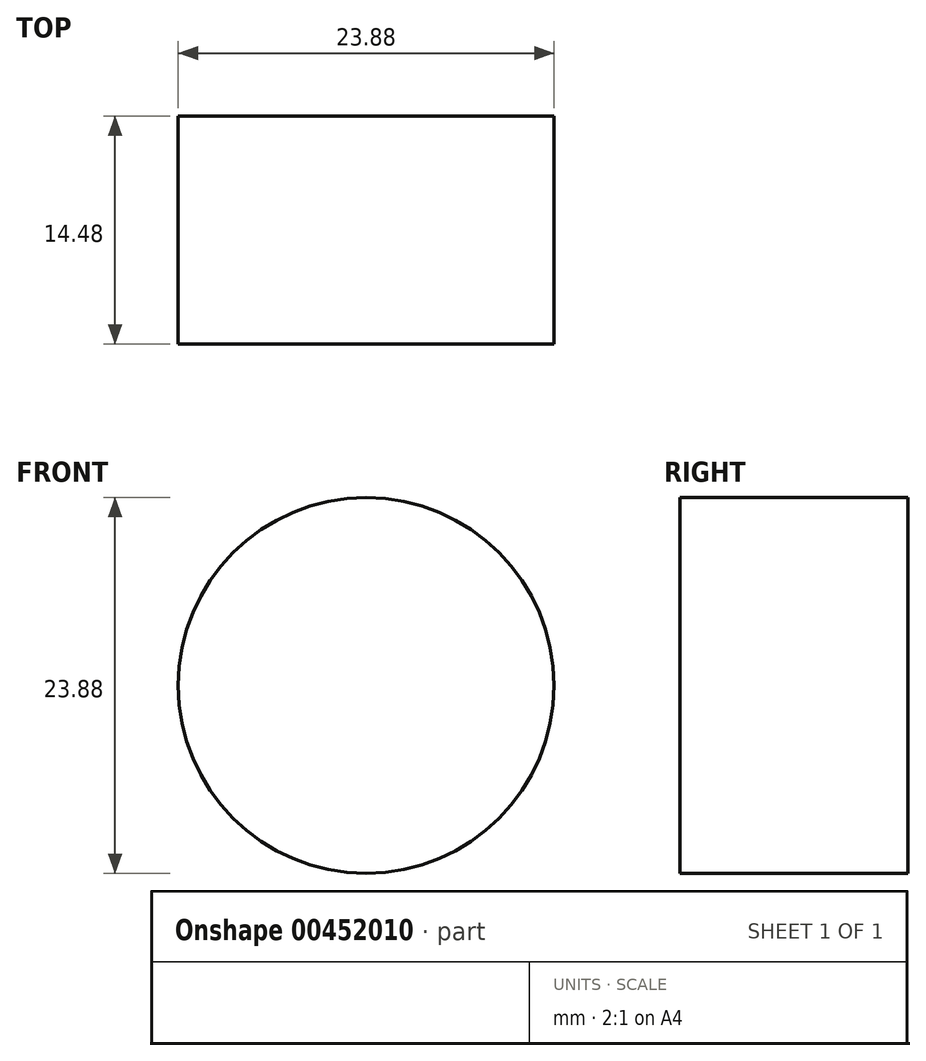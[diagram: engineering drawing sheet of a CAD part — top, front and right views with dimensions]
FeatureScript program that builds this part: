
annotation { "Feature Type Name" : "Feature", "Feature Type Description" : "" }
export const myFeature = defineFeature(function(context is Context, id is Id, definition is map)
    precondition{}
    {
        {
            var Q0;
            Q0=qCreatedBy(makeId("Front.planeOp"),FACE);
            var sketch = newSketch(context, id + "F0", { "sketchPlane" : qUnion([Q0])});
            skCircle(sketch, "E0", {"center": v(0, 0) * mm, "radius": 11.94 * mm});
            skSolve(sketch);
        }
        {
            var Q0;
            Q0=qSketchRegion(id+"F0",true);
            extrude(context, id + "F1", {"entities" : qUnion([Q0]), "depth" : 14.48 * mm});
        }
    });
